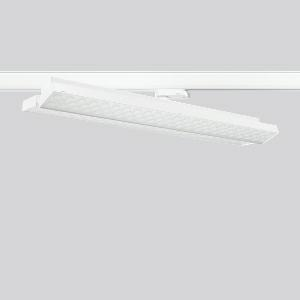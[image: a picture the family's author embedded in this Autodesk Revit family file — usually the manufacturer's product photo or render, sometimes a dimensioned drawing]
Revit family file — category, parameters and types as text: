
# Revit family: tx-move_742161_002_76_2d49
name_source: partatom
category: Lighting Fixtures
units: mm (PartAtom-declared; Revit-internal decimal feet)

## family parameters
Cut with Voids When Loaded = No
Host = Face
Light Source = No
Part Type = Normal
Room Calculation Point = No
Round Connector Dimension = Use Diameter
Shared = No

## types (1)
- MultiLumen 1 (1 x LED Modul 830, 2900 lm, 3000)
    Apparent Load = 41 VA
    CIE Flux Codes = 90 97 99 100 100
    Color Rendering = 80
    Color Temperature = 3000
    Default Elevation = 1800 mm
    Description = Series: TX-MOVE
Multifunctional surface-mounted spotlight for area lighting. Very flat design. Housing: sheet steel, powder-coated. Rotation range: 356°. Swivel range: 90°. Consistent alignment possible with visible tilt scale. High-efficiency LED units with optimum light control thanks to clear plastic (PC) lens optics. Spezielle Mikrostrukturen reduzieren Gelbsaum. Symmetrical light distribution. With adapter for RZB 3-circuit DALI tracks. Suitable for Track on ceiling. MultiLumen: Luminous flux adjustable in 3 steps. Factory setting is the highest luminous flux. Environmentally friendly and resource-saving due to replaceable and recyclable components. Very good glare control, ideal for till areas. 
Colour: traffic white, matt (RAL 9016)
Length: 570 mm
Width: 119 mm
Height: 88 mm
Lamp: LED
Socket: without socket
Colour temperature: 3000K
Colour rendering index (CRI): 80
System power: 41 W
Rated luminous flux: 5800 lm
Luminous efficiency: 141 lm/W
System power 2: 57 W
Rated luminous flux 2: 7850 lm
Luminous efficiency 2: 138 lm/W
System power 3: 73 W
Rated luminous flux 3: 9600 lm
Luminous efficiency 3: 132 lm/W
Control gear: Dimmable EVG, DALI
Protection class: I
Type of protection: IP 20
    Height = 75 mm
    Lamp = 1 x LED Modul 830
    Lamp Light Flux = 2900 lm
    Lamp count = 1
    Length = 569 mm
    Lifetime = 50000 h
    Luminous efficacy = 141 lm/W
    Manufacturer = RZB
    ModVariant = No
    Model = 742161.002.76
    Mounting Place = Ceiling
    Mounting Type = Surface mounted
    Number of Poles = 1
    OnlyDefault = Yes
    Power Factor = 1
    Product Name = TX-MOVE
    Product group = Track mounted projectors
    ProductGroupID = 301
    Protection Class = Protection class I
    Protection Degree = IP 20
    RLX_Detail_Level = 1
    RLX_Emergency_Light_Flux = 0 lm
    RLX_Emergency_Type = 0
    RLX_Emergency_Type_DB = No
    RlxData = <blob elided: 31025 chars, md5=55998005>
    Socket = socket
    Standby Power = 0 W
    System Light Flux = 5800 lm
    System Power = 41 W
    Type Comments = MultiLumen 1
    Type Image = 742162.002.jpg
    URL = http://relux.com
    VarID = multilumen_1
    Voltage = 0 V
    Weight = 0.00 kg
    Width = 119 mm

## geometry (parser evidence)
native form markers: Blend x4, Sweep x15
no freeform markers — native parametric forms only
